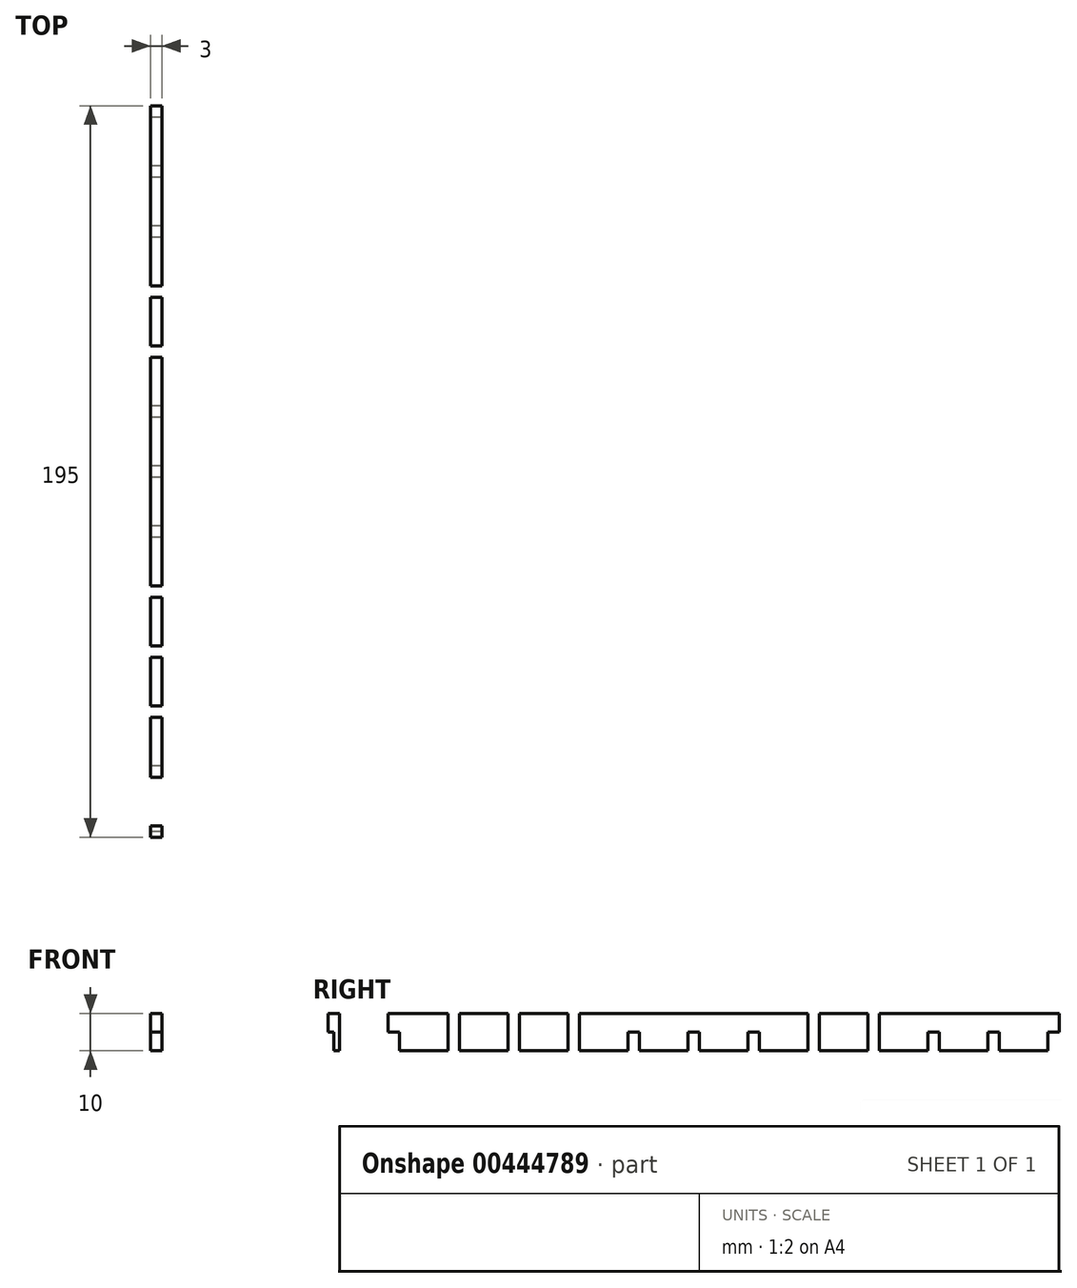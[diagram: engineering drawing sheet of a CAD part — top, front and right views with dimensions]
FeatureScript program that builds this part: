
annotation { "Feature Type Name" : "Feature", "Feature Type Description" : "" }
export const myFeature = defineFeature(function(context is Context, id is Id, definition is map)
    precondition{}
    {
        {
            var Q0;
            Q0=qCreatedBy(makeId("Right.planeOp"),FACE);
            var sketch = newSketch(context, id + "F0", { "sketchPlane" : qUnion([Q0])});
            skLineSegment(sketch, "E0", {"start": v(0, 0) * mm, "end": v(11.5, 0) * mm});
            skLineSegment(sketch, "E1", {"start": v(11.5, 0) * mm, "end": v(11.5, -2) * mm});
            skLineSegment(sketch, "E2", {"start": v(11.5, -2) * mm, "end": v(20.5, -2) * mm});
            skLineSegment(sketch, "E3", {"start": v(20.5, -2) * mm, "end": v(20.5, 0) * mm});
            skLineSegment(sketch, "E4", {"start": v(20.5, 0) * mm, "end": v(43.5, 0) * mm});
            skLineSegment(sketch, "E5", {"start": v(43.5, 0) * mm, "end": v(43.5, -2) * mm});
            skLineSegment(sketch, "E6", {"start": v(43.5, -2) * mm, "end": v(52.5, -2) * mm});
            skLineSegment(sketch, "E7", {"start": v(52.5, -2) * mm, "end": v(52.5, 0) * mm});
            skLineSegment(sketch, "E8", {"start": v(0, 0) * mm, "end": v(0, 10) * mm});
            skPoint(sketch, "E9.oppositeSnap0", {"position": v(0, 5) * mm});
            skLineSegment(sketch, "E9.bottom", {"start": v(0, 10) * mm, "end": v(-1.5, 10) * mm});
            skLineSegment(sketch, "E9.top", {"start": v(0, 5) * mm, "end": v(-1.5, 5) * mm});
            skLineSegment(sketch, "E9.left", {"start": v(0, 10) * mm, "end": v(0, 5) * mm});
            skLineSegment(sketch, "E9.right", {"start": v(-1.5, 10) * mm, "end": v(-1.5, 5) * mm});
            skLineSegment(sketch, "E10.bottom", {"start": v(14.5, 10) * mm, "end": v(17.5, 10) * mm});
            skLineSegment(sketch, "E10.top", {"start": v(14.5, 5) * mm, "end": v(17.5, 5) * mm});
            skLineSegment(sketch, "E10.left", {"start": v(14.5, 10) * mm, "end": v(14.5, 5) * mm});
            skLineSegment(sketch, "E10.right", {"start": v(17.5, 10) * mm, "end": v(17.5, 5) * mm});
            skLineSegment(sketch, "E11.top", {"start": v(0, 0) * mm, "end": v(-1.5, 0) * mm});
            skLineSegment(sketch, "E11.left", {"start": v(0, 5) * mm, "end": v(0, 0) * mm});
            skLineSegment(sketch, "E11.right", {"start": v(-1.5, 5) * mm, "end": v(-1.5, 0) * mm});
            skLineSegment(sketch, "E12.top", {"start": v(14.5, -2) * mm, "end": v(17.5, -2) * mm});
            skLineSegment(sketch, "E12.left", {"start": v(14.5, 5) * mm, "end": v(14.5, -2) * mm});
            skLineSegment(sketch, "E12.right", {"start": v(17.5, 5) * mm, "end": v(17.5, -2) * mm});
            skLineSegment(sketch, "E13.bottom", {"start": v(0, 10) * mm, "end": v(1.5, 10) * mm});
            skLineSegment(sketch, "E13.top", {"start": v(0, 5) * mm, "end": v(1.5, 5) * mm});
            skLineSegment(sketch, "E13.right", {"start": v(1.5, 10) * mm, "end": v(1.5, 5) * mm});
            skLineSegment(sketch, "E14.top", {"start": v(0, 0) * mm, "end": v(1.5, 0) * mm});
            skLineSegment(sketch, "E14.right", {"start": v(1.5, 5) * mm, "end": v(1.5, 0) * mm});
            skLineSegment(sketch, "E15.bottom", {"start": v(11.5, 10) * mm, "end": v(20.5, 10) * mm});
            skLineSegment(sketch, "E15.top", {"start": v(11.5, 13) * mm, "end": v(20.5, 13) * mm});
            skLineSegment(sketch, "E15.left", {"start": v(11.5, 10) * mm, "end": v(11.5, 13) * mm});
            skLineSegment(sketch, "E15.right", {"start": v(20.5, 10) * mm, "end": v(20.5, 13) * mm});
            skLineSegment(sketch, "E16", {"start": v(52.5, 0) * mm, "end": v(75.5, 0) * mm});
            skLineSegment(sketch, "E17", {"start": v(75.5, 0) * mm, "end": v(75.5, -2) * mm});
            skLineSegment(sketch, "E18", {"start": v(75.5, -2) * mm, "end": v(84.5, -2) * mm});
            skLineSegment(sketch, "E19", {"start": v(84.5, -2) * mm, "end": v(84.5, 0) * mm});
            skLineSegment(sketch, "E20", {"start": v(84.5, 0) * mm, "end": v(96, 0) * mm});
            skLineSegment(sketch, "E21", {"start": v(96, 0) * mm, "end": v(96, 19.13) * mm, "construction": true});
            skLineSegment(sketch, "E22", {"start": v(16, 10) * mm, "end": v(16, 11.65) * mm, "construction": true});
            skLineSegment(sketch, "E23.bottom", {"start": v(30.5, 0) * mm, "end": v(33.5, 0) * mm});
            skLineSegment(sketch, "E23.top", {"start": v(30.5, 5) * mm, "end": v(33.5, 5) * mm});
            skLineSegment(sketch, "E23.left", {"start": v(30.5, 0) * mm, "end": v(30.5, 5) * mm});
            skLineSegment(sketch, "E23.right", {"start": v(33.5, 0) * mm, "end": v(33.5, 5) * mm});
            skLineSegment(sketch, "E24.bottom", {"start": v(33.5, 5) * mm, "end": v(30.5, 5) * mm});
            skLineSegment(sketch, "E24.top", {"start": v(33.5, 10) * mm, "end": v(30.5, 10) * mm});
            skLineSegment(sketch, "E24.left", {"start": v(33.5, 5) * mm, "end": v(33.5, 10) * mm});
            skLineSegment(sketch, "E24.right", {"start": v(30.5, 5) * mm, "end": v(30.5, 10) * mm});
            skLineSegment(sketch, "E25", {"start": v(32, 0) * mm, "end": v(32, 2.31) * mm, "construction": true});
            skLineSegment(sketch, "E26.bottom", {"start": v(46.5, -2) * mm, "end": v(49.5, -2) * mm});
            skLineSegment(sketch, "E26.top", {"start": v(46.5, 5) * mm, "end": v(49.5, 5) * mm});
            skLineSegment(sketch, "E26.left", {"start": v(46.5, -2) * mm, "end": v(46.5, 5) * mm});
            skLineSegment(sketch, "E26.right", {"start": v(49.5, -2) * mm, "end": v(49.5, 5) * mm});
            skLineSegment(sketch, "E27.bottom", {"start": v(49.5, 5) * mm, "end": v(46.5, 5) * mm});
            skLineSegment(sketch, "E27.top", {"start": v(49.5, 10) * mm, "end": v(46.5, 10) * mm});
            skLineSegment(sketch, "E27.left", {"start": v(49.5, 5) * mm, "end": v(49.5, 10) * mm});
            skLineSegment(sketch, "E27.right", {"start": v(46.5, 5) * mm, "end": v(46.5, 10) * mm});
            skLineSegment(sketch, "E28.bottom", {"start": v(62.5, 0) * mm, "end": v(65.5, 0) * mm});
            skLineSegment(sketch, "E28.top", {"start": v(62.5, 5) * mm, "end": v(65.5, 5) * mm});
            skLineSegment(sketch, "E28.left", {"start": v(62.5, 0) * mm, "end": v(62.5, 5) * mm});
            skLineSegment(sketch, "E28.right", {"start": v(65.5, 0) * mm, "end": v(65.5, 5) * mm});
            skLineSegment(sketch, "E29.bottom", {"start": v(65.5, 5) * mm, "end": v(62.5, 5) * mm});
            skLineSegment(sketch, "E29.top", {"start": v(65.5, 10) * mm, "end": v(62.5, 10) * mm});
            skLineSegment(sketch, "E29.left", {"start": v(65.5, 5) * mm, "end": v(65.5, 10) * mm});
            skLineSegment(sketch, "E29.right", {"start": v(62.5, 5) * mm, "end": v(62.5, 10) * mm});
            skLineSegment(sketch, "E30.bottom", {"start": v(81.5, -2) * mm, "end": v(78.5, -2) * mm});
            skLineSegment(sketch, "E30.top", {"start": v(81.5, 5) * mm, "end": v(78.5, 5) * mm});
            skLineSegment(sketch, "E30.left", {"start": v(81.5, -2) * mm, "end": v(81.5, 5) * mm});
            skLineSegment(sketch, "E30.right", {"start": v(78.5, -2) * mm, "end": v(78.5, 5) * mm});
            skLineSegment(sketch, "E31.top", {"start": v(81.5, 10) * mm, "end": v(78.5, 10) * mm});
            skLineSegment(sketch, "E31.left", {"start": v(81.5, 5) * mm, "end": v(81.5, 10) * mm});
            skLineSegment(sketch, "E31.right", {"start": v(78.5, 5) * mm, "end": v(78.5, 10) * mm});
            skLineSegment(sketch, "E32.bottom", {"start": v(96, 0) * mm, "end": v(94.5, 0) * mm});
            skLineSegment(sketch, "E32.top", {"start": v(96, 5) * mm, "end": v(94.5, 5) * mm});
            skLineSegment(sketch, "E32.left", {"start": v(96, 0) * mm, "end": v(96, 5) * mm});
            skLineSegment(sketch, "E32.right", {"start": v(94.5, 0) * mm, "end": v(94.5, 5) * mm});
            skLineSegment(sketch, "E33.left", {"start": v(96, 5) * mm, "end": v(96, 5) * mm});
            skLineSegment(sketch, "E33.right", {"start": v(94.5, 5) * mm, "end": v(94.5, 5) * mm});
            skLineSegment(sketch, "E34.top", {"start": v(96, 10) * mm, "end": v(94.5, 10) * mm});
            skLineSegment(sketch, "E34.left", {"start": v(96, 5) * mm, "end": v(96, 10) * mm});
            skLineSegment(sketch, "E34.right", {"start": v(94.5, 5) * mm, "end": v(94.5, 10) * mm});
            skLineSegment(sketch, "E35", {"start": v(48, -2) * mm, "end": v(48, 0) * mm, "construction": true});
            skLineSegment(sketch, "E36", {"start": v(64, 0) * mm, "end": v(64, 2.67) * mm, "construction": true});
            skLineSegment(sketch, "E37", {"start": v(80, -2) * mm, "end": v(80, 0) * mm, "construction": true});
            skLineSegment(sketch, "E38", {"start": v(1.5, 10) * mm, "end": v(96, 10) * mm});
            skLineSegment(sketch, "E39.MirrorCS", {"start": v(96, 5) * mm, "end": v(97.5, 5) * mm});
            skLineSegment(sketch, "E40.MirrorCS", {"start": v(145.5, 5) * mm, "end": v(142.5, 5) * mm});
            skLineSegment(sketch, "E41.MirrorCS", {"start": v(110.5, 5) * mm, "end": v(113.5, 5) * mm});
            skLineSegment(sketch, "E42.MirrorCS", {"start": v(129.5, 5) * mm, "end": v(126.5, 5) * mm});
            skLineSegment(sketch, "E43.MirrorCS", {"start": v(177.5, 5) * mm, "end": v(174.5, 5) * mm});
            skLineSegment(sketch, "E44.MirrorCS", {"start": v(192, 5) * mm, "end": v(190.5, 5) * mm});
            skLineSegment(sketch, "E45.MirrorCS", {"start": v(192, 5) * mm, "end": v(193.5, 5) * mm});
            skLineSegment(sketch, "E46.MirrorCS", {"start": v(142.5, 5) * mm, "end": v(145.5, 5) * mm});
            skLineSegment(sketch, "E47.MirrorCS", {"start": v(126.5, 5) * mm, "end": v(129.5, 5) * mm});
            skLineSegment(sketch, "E48.MirrorCS", {"start": v(192, 10) * mm, "end": v(190.5, 10) * mm});
            skLineSegment(sketch, "E49.MirrorCS", {"start": v(171.5, -2) * mm, "end": v(171.5, 0) * mm});
            skLineSegment(sketch, "E50.MirrorCS", {"start": v(180.5, 0) * mm, "end": v(180.5, -2) * mm});
            skLineSegment(sketch, "E51.MirrorCS", {"start": v(177.5, 10) * mm, "end": v(174.5, 10) * mm});
            skLineSegment(sketch, "E52.MirrorCS", {"start": v(116.5, 0) * mm, "end": v(116.5, -2) * mm});
            skLineSegment(sketch, "E53.MirrorCS", {"start": v(177.5, -2) * mm, "end": v(174.5, -2) * mm});
            skLineSegment(sketch, "E54.MirrorCS", {"start": v(192, 0) * mm, "end": v(190.5, 0) * mm});
            skLineSegment(sketch, "E55.MirrorCS", {"start": v(126.5, 10) * mm, "end": v(129.5, 10) * mm});
            skLineSegment(sketch, "E56.MirrorCS", {"start": v(145.5, -2) * mm, "end": v(142.5, -2) * mm});
            skLineSegment(sketch, "E57.MirrorCS", {"start": v(110.5, -2) * mm, "end": v(113.5, -2) * mm});
            skLineSegment(sketch, "E58.MirrorCS", {"start": v(192, 0) * mm, "end": v(193.5, 0) * mm});
            skLineSegment(sketch, "E59.MirrorCS", {"start": v(96, 10) * mm, "end": v(97.5, 10) * mm});
            skLineSegment(sketch, "E60.MirrorCS", {"start": v(110.5, 10) * mm, "end": v(113.5, 10) * mm});
            skLineSegment(sketch, "E61.MirrorCS", {"start": v(142.5, 10) * mm, "end": v(145.5, 10) * mm});
            skLineSegment(sketch, "E62.MirrorCS", {"start": v(107.5, -2) * mm, "end": v(107.5, 0) * mm});
            skLineSegment(sketch, "E63.MirrorCS", {"start": v(192, 10) * mm, "end": v(193.5, 10) * mm});
            skLineSegment(sketch, "E64.MirrorCS", {"start": v(96, 0) * mm, "end": v(97.5, 0) * mm});
            skLineSegment(sketch, "E65.MirrorCS", {"start": v(139.5, -2) * mm, "end": v(139.5, 0) * mm});
            skLineSegment(sketch, "E66.MirrorCS", {"start": v(129.5, 0) * mm, "end": v(126.5, 0) * mm});
            skLineSegment(sketch, "E67.MirrorCS", {"start": v(148.5, 0) * mm, "end": v(148.5, -2) * mm});
            skLineSegment(sketch, "E68.MirrorCS", {"start": v(192, 5) * mm, "end": v(192, 0) * mm});
            skLineSegment(sketch, "E69.MirrorCS", {"start": v(112, -2) * mm, "end": v(112, 0) * mm, "construction": true});
            skLineSegment(sketch, "E70.MirrorCS", {"start": v(176, 10) * mm, "end": v(176, 11.65) * mm, "construction": true});
            skLineSegment(sketch, "E71.MirrorCS", {"start": v(192, 10) * mm, "end": v(192, 5) * mm});
            skLineSegment(sketch, "E72.MirrorCS", {"start": v(161.5, 0) * mm, "end": v(158.5, 0) * mm});
            skLineSegment(sketch, "E73.MirrorCS", {"start": v(128, 0) * mm, "end": v(128, 2.67) * mm, "construction": true});
            skLineSegment(sketch, "E74.MirrorCS", {"start": v(160, 0) * mm, "end": v(160, 2.31) * mm, "construction": true});
            skLineSegment(sketch, "E75.MirrorCS", {"start": v(144, -2) * mm, "end": v(144, 0) * mm, "construction": true});
            skLineSegment(sketch, "E76.MirrorCS", {"start": v(161.5, 5) * mm, "end": v(158.5, 5) * mm});
            skLineSegment(sketch, "E77.MirrorCS", {"start": v(171.5, 0) * mm, "end": v(148.5, 0) * mm});
            skLineSegment(sketch, "E78.MirrorCS", {"start": v(180.5, -2) * mm, "end": v(171.5, -2) * mm});
            skLineSegment(sketch, "E79.MirrorCS", {"start": v(192, 0) * mm, "end": v(180.5, 0) * mm});
            skLineSegment(sketch, "E80.MirrorCS", {"start": v(177.5, 10) * mm, "end": v(177.5, 5) * mm});
            skLineSegment(sketch, "E81.MirrorCS", {"start": v(158.5, 0) * mm, "end": v(158.5, 5) * mm});
            skLineSegment(sketch, "E82.MirrorCS", {"start": v(129.5, 0) * mm, "end": v(129.5, 5) * mm});
            skLineSegment(sketch, "E83.MirrorCS", {"start": v(97.5, 5) * mm, "end": v(97.5, 10) * mm});
            skPoint(sketch, "E84.MirrorP", {"position": v(192, 5) * mm});
            skLineSegment(sketch, "E85.MirrorCS", {"start": v(139.5, 0) * mm, "end": v(116.5, 0) * mm});
            skLineSegment(sketch, "E86.MirrorCS", {"start": v(126.5, 5) * mm, "end": v(126.5, 10) * mm});
            skLineSegment(sketch, "E87.MirrorCS", {"start": v(161.5, 5) * mm, "end": v(161.5, 10) * mm});
            skLineSegment(sketch, "E88.MirrorCS", {"start": v(180.5, 10) * mm, "end": v(180.5, 13) * mm});
            skLineSegment(sketch, "E89.MirrorCS", {"start": v(180.5, 13) * mm, "end": v(171.5, 13) * mm});
            skLineSegment(sketch, "E90.MirrorCS", {"start": v(158.5, 5) * mm, "end": v(158.5, 10) * mm});
            skLineSegment(sketch, "E91.MirrorCS", {"start": v(161.5, 0) * mm, "end": v(161.5, 5) * mm});
            skLineSegment(sketch, "E92.MirrorCS", {"start": v(107.5, 0) * mm, "end": v(96, 0) * mm});
            skLineSegment(sketch, "E93.MirrorCS", {"start": v(142.5, 5) * mm, "end": v(142.5, 10) * mm});
            skLineSegment(sketch, "E94.MirrorCS", {"start": v(193.5, 5) * mm, "end": v(193.5, 0) * mm});
            skLineSegment(sketch, "E95.MirrorCS", {"start": v(110.5, 5) * mm, "end": v(110.5, 10) * mm});
            skLineSegment(sketch, "E96.MirrorCS", {"start": v(180.5, 10) * mm, "end": v(171.5, 10) * mm});
            skLineSegment(sketch, "E97.MirrorCS", {"start": v(158.5, 10) * mm, "end": v(161.5, 10) * mm});
            skLineSegment(sketch, "E98.MirrorCS", {"start": v(145.5, 5) * mm, "end": v(145.5, 10) * mm});
            skLineSegment(sketch, "E99.MirrorCS", {"start": v(113.5, -2) * mm, "end": v(113.5, 5) * mm});
            skLineSegment(sketch, "E100.MirrorCS", {"start": v(174.5, 5) * mm, "end": v(174.5, -2) * mm});
            skLineSegment(sketch, "E101.MirrorCS", {"start": v(142.5, -2) * mm, "end": v(142.5, 5) * mm});
            skLineSegment(sketch, "E102.MirrorCS", {"start": v(113.5, 5) * mm, "end": v(113.5, 10) * mm});
            skLineSegment(sketch, "E103.MirrorCS", {"start": v(190.5, 10) * mm, "end": v(96, 10) * mm});
            skLineSegment(sketch, "E104.MirrorCS", {"start": v(190.5, 5) * mm, "end": v(190.5, 0) * mm});
            skLineSegment(sketch, "E105.MirrorCS", {"start": v(158.5, 5) * mm, "end": v(161.5, 5) * mm});
            skLineSegment(sketch, "E106.MirrorCS", {"start": v(126.5, 0) * mm, "end": v(126.5, 5) * mm});
            skLineSegment(sketch, "E107.MirrorCS", {"start": v(97.5, 0) * mm, "end": v(97.5, 5) * mm});
            skLineSegment(sketch, "E108.MirrorCS", {"start": v(174.5, 10) * mm, "end": v(174.5, 5) * mm});
            skLineSegment(sketch, "E109.MirrorCS", {"start": v(110.5, -2) * mm, "end": v(110.5, 5) * mm});
            skLineSegment(sketch, "E110.MirrorCS", {"start": v(177.5, 5) * mm, "end": v(177.5, -2) * mm});
            skLineSegment(sketch, "E111.MirrorCS", {"start": v(116.5, -2) * mm, "end": v(107.5, -2) * mm});
            skLineSegment(sketch, "E112.MirrorCS", {"start": v(145.5, -2) * mm, "end": v(145.5, 5) * mm});
            skLineSegment(sketch, "E113.MirrorCS", {"start": v(193.5, 10) * mm, "end": v(193.5, 5) * mm});
            skLineSegment(sketch, "E114.MirrorCS", {"start": v(129.5, 5) * mm, "end": v(129.5, 10) * mm});
            skLineSegment(sketch, "E115.MirrorCS", {"start": v(192, 0) * mm, "end": v(192, 10) * mm});
            skLineSegment(sketch, "E116.MirrorCS", {"start": v(148.5, -2) * mm, "end": v(139.5, -2) * mm});
            skLineSegment(sketch, "E117.MirrorCS", {"start": v(171.5, 10) * mm, "end": v(171.5, 13) * mm});
            skLineSegment(sketch, "E118.MirrorCS", {"start": v(190.5, 10) * mm, "end": v(190.5, 5) * mm});
            skLineSegment(sketch, "E119.top", {"start": v(14.5, 13) * mm, "end": v(17.5, 13) * mm});
            skLineSegment(sketch, "E119.left", {"start": v(14.5, 10) * mm, "end": v(14.5, 13) * mm});
            skLineSegment(sketch, "E119.right", {"start": v(17.5, 10) * mm, "end": v(17.5, 13) * mm});
            skLineSegment(sketch, "E120.bottom", {"start": v(174.5, 10) * mm, "end": v(177.5, 10) * mm});
            skLineSegment(sketch, "E120.top", {"start": v(174.5, 13) * mm, "end": v(177.5, 13) * mm});
            skLineSegment(sketch, "E120.left", {"start": v(174.5, 10) * mm, "end": v(174.5, 13) * mm});
            skLineSegment(sketch, "E120.right", {"start": v(177.5, 10) * mm, "end": v(177.5, 13) * mm});
            skLineSegment(sketch, "E121", {"start": v(11.5, 0) * mm, "end": v(180.5, 0) * mm});
            skSolve(sketch);
        }
        {
            var Q0;
            {var subQ5=sQuery(id+"F0.wireOp",EDGE,"E0");Q0=makeQuery(id+"F0.imprint","IMPRINT",FACE,{"disambiguationData":[TD([[makeQuery(id+"F0.imprint","IMPRINT",EDGE,{"derivedFrom":subQ5}),1.0]])]});}
            var Q1;
            {var subQ2=sQuery(id+"F0.wireOp",EDGE,"E10.right");Q1=makeQuery(id+"F0.imprint","IMPRINT",FACE,{"disambiguationData":[TD([[makeQuery(id+"F0.imprint","IMPRINT",EDGE,{"derivedFrom":subQ2}),1.0]])]});}
            var Q2;
            Q2=makeQuery(id+"F0.imprint","IMPRINT",FACE,{"disambiguationData":[TD([[makeQuery(id+"F0.imprint","IMPRINT",EDGE,{"derivedFrom":sQuery(id+"F0.wireOp",EDGE,"E13.bottom")}),-1.0]])]});
            var Q3;
            Q3=makeQuery(id+"F0.imprint","IMPRINT",FACE,{"disambiguationData":[TD([[makeQuery(id+"F0.imprint","IMPRINT",EDGE,{"derivedFrom":sQuery(id+"F0.wireOp",EDGE,"E9.bottom")}),1.0]])]});
            var Q4;
            Q4=makeQuery(id+"F0.imprint","IMPRINT",FACE,{"disambiguationData":[TD([[makeQuery(id+"F0.imprint","IMPRINT",EDGE,{"derivedFrom":sQuery(id+"F0.wireOp",EDGE,"E10.left")}),1.0]])]});
            var Q5;
            Q5=makeQuery(id+"F0.imprint","IMPRINT",FACE,{"disambiguationData":[TD([[makeQuery(id+"F0.imprint","IMPRINT",EDGE,{"derivedFrom":sQuery(id+"F0.wireOp",EDGE,"E24.bottom")}),-1.0]])]});
            var Q6;
            Q6=makeQuery(id+"F0.imprint","IMPRINT",FACE,{"disambiguationData":[TD([[makeQuery(id+"F0.imprint","IMPRINT",EDGE,{"derivedFrom":sQuery(id+"F0.wireOp",EDGE,"E27.bottom")}),-1.0]])]});
            var Q7;
            Q7=makeQuery(id+"F0.imprint","IMPRINT",FACE,{"disambiguationData":[TD([[makeQuery(id+"F0.imprint","IMPRINT",EDGE,{"derivedFrom":sQuery(id+"F0.wireOp",EDGE,"E29.bottom")}),-1.0]])]});
            var Q8;
            Q8=makeQuery(id+"F0.imprint","IMPRINT",FACE,{"disambiguationData":[TD([[makeQuery(id+"F0.imprint","IMPRINT",EDGE,{"derivedFrom":sQuery(id+"F0.wireOp",EDGE,"E30.top")}),-1.0]])]});
            var Q9;
            Q9=makeQuery(id+"F0.imprint","IMPRINT",FACE,{"disambiguationData":[TD([[makeQuery(id+"F0.imprint","IMPRINT",EDGE,{"derivedFrom":sQuery(id+"F0.wireOp",EDGE,"E32.top")}),-1.0]])]});
            var Q10;
            Q10=makeQuery(id+"F0.imprint","IMPRINT",FACE,{"disambiguationData":[TD([[makeQuery(id+"F0.imprint","IMPRINT",EDGE,{"derivedFrom":sQuery(id+"F0.wireOp",EDGE,"E39.MirrorCS")}),1.0]])]});
            var Q11;
            Q11=makeQuery(id+"F0.imprint","IMPRINT",FACE,{"disambiguationData":[TD([[makeQuery(id+"F0.imprint","IMPRINT",EDGE,{"derivedFrom":sQuery(id+"F0.wireOp",EDGE,"E41.MirrorCS")}),1.0]])]});
            var Q12;
            Q12=makeQuery(id+"F0.imprint","IMPRINT",FACE,{"disambiguationData":[TD([[makeQuery(id+"F0.imprint","IMPRINT",EDGE,{"derivedFrom":sQuery(id+"F0.wireOp",EDGE,"E47.MirrorCS")}),1.0]])]});
            var Q13;
            Q13=makeQuery(id+"F0.imprint","IMPRINT",FACE,{"disambiguationData":[TD([[makeQuery(id+"F0.imprint","IMPRINT",EDGE,{"derivedFrom":sQuery(id+"F0.wireOp",EDGE,"E46.MirrorCS")}),1.0]])]});
            var Q14;
            {var subQ0=sQuery(id+"F0.wireOp",EDGE,"E87.MirrorCS");Q14=makeQuery(id+"F0.imprint","IMPRINT",FACE,{"disambiguationData":[TD([[makeQuery(id+"F0.imprint","IMPRINT",EDGE,{"derivedFrom":subQ0}),1.0]])]});}
            var Q15;
            Q15=makeQuery(id+"F0.imprint","IMPRINT",FACE,{"disambiguationData":[TD([[makeQuery(id+"F0.imprint","IMPRINT",EDGE,{"derivedFrom":sQuery(id+"F0.wireOp",EDGE,"E43.MirrorCS")}),-1.0]])]});
            var Q16;
            {var subQ0=sQuery(id+"F0.wireOp",EDGE,"E44.MirrorCS");Q16=makeQuery(id+"F0.imprint","IMPRINT",FACE,{"disambiguationData":[TD([[makeQuery(id+"F0.imprint","IMPRINT",EDGE,{"derivedFrom":subQ0}),-1.0]])]});}
            var Q17;
            {var subQ0=sQuery(id+"F0.wireOp",EDGE,"E45.MirrorCS");Q17=makeQuery(id+"F0.imprint","IMPRINT",FACE,{"disambiguationData":[TD([[makeQuery(id+"F0.imprint","IMPRINT",EDGE,{"derivedFrom":subQ0}),1.0]])]});}
            var Q18;
            {var subQ1=sQuery(id+"F0.wireOp",EDGE,"E23.right");Q18=makeQuery(id+"F0.imprint","IMPRINT",FACE,{"disambiguationData":[TD([[makeQuery(id+"F0.imprint","IMPRINT",EDGE,{"derivedFrom":subQ1}),-1.0]])]});}
            var Q19;
            {var subQ2=sQuery(id+"F0.wireOp",EDGE,"E27.left");Q19=makeQuery(id+"F0.imprint","IMPRINT",FACE,{"disambiguationData":[TD([[makeQuery(id+"F0.imprint","IMPRINT",EDGE,{"derivedFrom":subQ2}),-1.0]])]});}
            var Q20;
            {var subQ1=sQuery(id+"F0.wireOp",EDGE,"E28.right");Q20=makeQuery(id+"F0.imprint","IMPRINT",FACE,{"disambiguationData":[TD([[makeQuery(id+"F0.imprint","IMPRINT",EDGE,{"derivedFrom":subQ1}),-1.0]])]});}
            var Q21;
            {var subQ2=sQuery(id+"F0.wireOp",EDGE,"E31.left");Q21=makeQuery(id+"F0.imprint","IMPRINT",FACE,{"disambiguationData":[TD([[makeQuery(id+"F0.imprint","IMPRINT",EDGE,{"derivedFrom":subQ2}),-1.0]])]});}
            var Q22;
            {var subQ2=sQuery(id+"F0.wireOp",EDGE,"E83.MirrorCS");Q22=makeQuery(id+"F0.imprint","IMPRINT",FACE,{"disambiguationData":[TD([[makeQuery(id+"F0.imprint","IMPRINT",EDGE,{"derivedFrom":subQ2}),-1.0]])]});}
            var Q23;
            {var subQ1=sQuery(id+"F0.wireOp",EDGE,"E86.MirrorCS");Q23=makeQuery(id+"F0.imprint","IMPRINT",FACE,{"disambiguationData":[TD([[makeQuery(id+"F0.imprint","IMPRINT",EDGE,{"derivedFrom":subQ1}),1.0]])]});}
            var Q24;
            {var subQ6=sQuery(id+"F0.wireOp",EDGE,"E82.MirrorCS");Q24=makeQuery(id+"F0.imprint","IMPRINT",FACE,{"disambiguationData":[TD([[makeQuery(id+"F0.imprint","IMPRINT",EDGE,{"derivedFrom":subQ6}),-1.0]])]});}
            var Q25;
            {var subQ7=sQuery(id+"F0.wireOp",EDGE,"E81.MirrorCS");Q25=makeQuery(id+"F0.imprint","IMPRINT",FACE,{"disambiguationData":[TD([[makeQuery(id+"F0.imprint","IMPRINT",EDGE,{"derivedFrom":subQ7}),1.0]])]});}
            var Q26;
            {var subQ7=sQuery(id+"F0.wireOp",EDGE,"E87.MirrorCS");Q26=makeQuery(id+"F0.imprint","IMPRINT",FACE,{"disambiguationData":[TD([[makeQuery(id+"F0.imprint","IMPRINT",EDGE,{"derivedFrom":subQ7}),-1.0]])]});}
            var Q27;
            {var subQ1=sQuery(id+"F0.wireOp",EDGE,"E80.MirrorCS");Q27=makeQuery(id+"F0.imprint","IMPRINT",FACE,{"disambiguationData":[TD([[makeQuery(id+"F0.imprint","IMPRINT",EDGE,{"derivedFrom":subQ1}),1.0]])]});}
            extrude(context, id + "F1", {"entities" : qUnion([Q0, Q1, Q2, Q3, Q4, Q5, Q6, Q7, Q8, Q9, Q10, Q11, Q12, Q13, Q14, Q15, Q16, Q17, Q18, Q19, Q20, Q21, Q22, Q23, Q24, Q25, Q26, Q27]), "depth" : 3 * mm});
        }
    });
